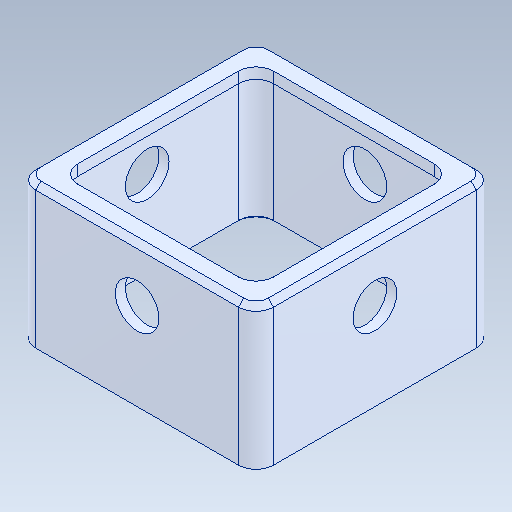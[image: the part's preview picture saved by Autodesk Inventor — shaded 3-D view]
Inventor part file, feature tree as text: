
AUTODESK INVENTOR PART (.ipt)
format: ipt  version: 2020 (Build 240168000, 168)  size: 138,240 bytes
history: native  units: in
note: dims shown in document units (in); Inventor stores cm internally (conversion verified against a paired STEP export)
features: chamfer x1
ambient origin geometry x8: Origin, YZ Plane, XZ Plane, XY Plane, X Axis, Y Axis, Z Axis, Center Point
bodies: Solid1 (feature_tree)
feature tree (1):
  chamfer  "Chamfer2"  [1 undecoded]
note: 1 required parameter value undecoded (feature->parameter linkage not recoverable at this tier; creation-order binding heuristic only, values carry confidence <= 0.55)
